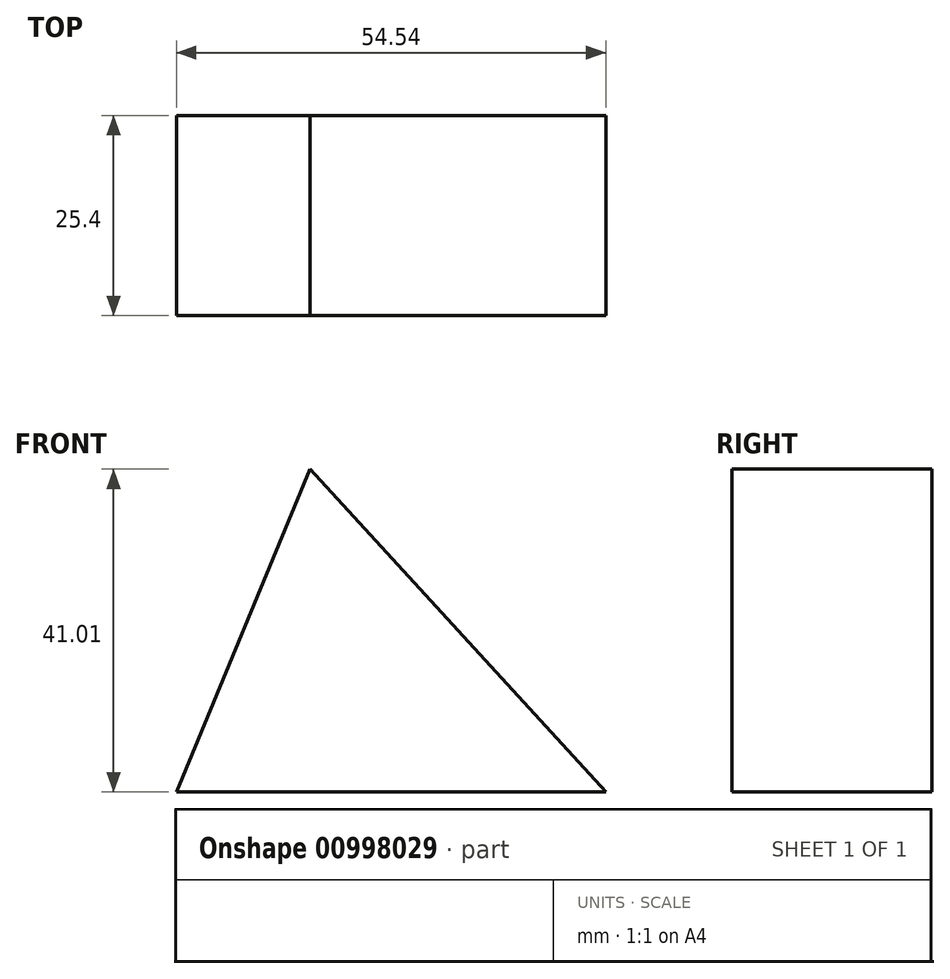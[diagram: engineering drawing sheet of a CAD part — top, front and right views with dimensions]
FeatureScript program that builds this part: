
annotation { "Feature Type Name" : "Feature", "Feature Type Description" : "" }
export const myFeature = defineFeature(function(context is Context, id is Id, definition is map)
    precondition{}
    {
        {
            var Q0;
            Q0=qCreatedBy(makeId("Front.planeOp"),FACE);
            var sketch = newSketch(context, id + "F0", { "sketchPlane" : qUnion([Q0])});
            skLineSegment(sketch, "E0", {"start": v(-37.56, 41.01) * mm, "end": v(0, 0) * mm});
            skLineSegment(sketch, "E1", {"start": v(0, 0) * mm, "end": v(-54.54, 0) * mm});
            skLineSegment(sketch, "E2", {"start": v(-54.54, 0) * mm, "end": v(-37.56, 41.01) * mm});
            skSolve(sketch);
        }
        {
            var Q0;
            Q0=makeQuery(id+"F0.imprint","IMPRINT",FACE,{"disambiguationData":[TD([[makeQuery(id+"F0.imprint","IMPRINT",EDGE,{"derivedFrom":sQuery(id+"F0.wireOp",EDGE,"E0")}),-1.0]])]});
            extrude(context, id + "F1", {"entities" : qUnion([Q0]), "depth" : 25.4 * mm, "offsetDistance" : 25.4 * mm});
        }
    });
